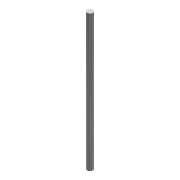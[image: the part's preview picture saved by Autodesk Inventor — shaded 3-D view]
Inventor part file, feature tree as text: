
AUTODESK INVENTOR PART (.ipt)
format: ipt  version: 2015 (Build 190159000, 159)  size: 87,552 bytes
history: native  units: mm
features: extrude x1, sketch x1
ambient origin geometry x8: Origin, YZ Plane, XZ Plane, XY Plane, X Axis, Y Axis, Z Axis, Center Point
bodies: Solid1 (feature_tree)
feature tree (2):
  extrude  "Extrusion1"  Depth=450.0mm TaperAngle=0.0deg
  sketch  "Sketch1"  dims[d0=19.0mm d1=450.0mm d2=0.0mm]
